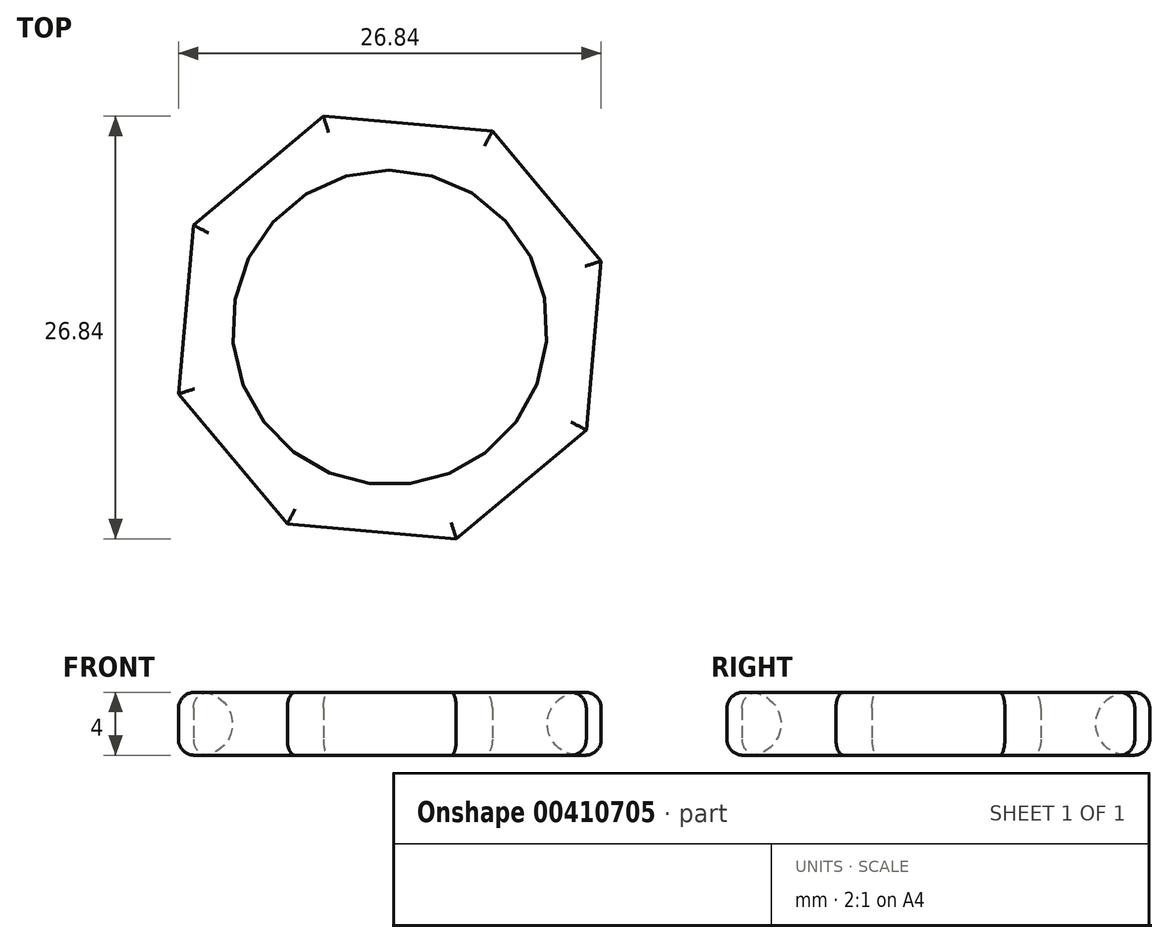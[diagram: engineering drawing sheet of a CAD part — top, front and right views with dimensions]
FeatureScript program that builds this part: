
annotation { "Feature Type Name" : "Feature", "Feature Type Description" : "" }
export const myFeature = defineFeature(function(context is Context, id is Id, definition is map)
    precondition{}
    {
        {
            var Q0;
            Q0=qCreatedBy(makeId("Top.planeOp"),FACE);
            var sketch = newSketch(context, id + "F0", { "sketchPlane" : qUnion([Q0])});
            skCircle(sketch, "E0.cCircle", {"center": v(0, 0) * mm, "radius": 13 * mm, "construction": true});
            skLineSegment(sketch, "E0.0", {"start": v(12.48, -6.5) * mm, "end": v(4.22, -13.42) * mm});
            skLineSegment(sketch, "E0.1", {"start": v(4.22, -13.42) * mm, "end": v(-6.5, -12.48) * mm});
            skLineSegment(sketch, "E0.2", {"start": v(-6.5, -12.48) * mm, "end": v(-13.42, -4.22) * mm});
            skLineSegment(sketch, "E0.3", {"start": v(-13.42, -4.22) * mm, "end": v(-12.48, 6.5) * mm});
            skLineSegment(sketch, "E0.4", {"start": v(-12.48, 6.5) * mm, "end": v(-4.22, 13.42) * mm});
            skLineSegment(sketch, "E0.5", {"start": v(-4.22, 13.42) * mm, "end": v(6.5, 12.48) * mm});
            skLineSegment(sketch, "E0.6", {"start": v(6.5, 12.48) * mm, "end": v(13.42, 4.22) * mm});
            skLineSegment(sketch, "E0.7", {"start": v(13.42, 4.22) * mm, "end": v(12.48, -6.5) * mm});
            skPoint(sketch, "E0.0.midPoint", {"position": v(8.35, -9.97) * mm});
            skCircle(sketch, "E1", {"center": v(0, 0) * mm, "radius": 10 * mm});
            skSolve(sketch);
        }
        {
            var Q0;
            Q0=makeQuery(id+"F0.imprint","IMPRINT",FACE,{"disambiguationData":[TD([[makeQuery(id+"F0.imprint","IMPRINT",EDGE,{"derivedFrom":sQuery(id+"F0.wireOp",EDGE,"E0.0")}),-1.0]])]});
            extrude(context, id + "F1", {"entities" : qUnion([Q0]), "depth" : 4 * mm});
        }
        {
            var Q0;
            Q0=makeQuery(id+"F1.opExtrude","CAP_EDGE",EDGE,{"disambiguationData":[OSD([sQuery(id+"F0.wireOp",EDGE,"E1")])],"isStart":true});
            var Q1;
            Q1=makeQuery(id+"F1.opExtrude","CAP_EDGE",EDGE,{"disambiguationData":[OSD([sQuery(id+"F0.wireOp",EDGE,"E1")])],"isStart":false});
            fillet(context, id + "F2", {"entities" : qUnion([Q0, Q1]), "radius" : 2 * mm, "tangentPropagation" : true, "allowEdgeOverflow" : false});
        }
        {
            var Q0;
            Q0=makeQuery(id+"F1.opExtrude","CAP_EDGE",EDGE,{"disambiguationData":[OSD([sQuery(id+"F0.wireOp",EDGE,"E0.5")])],"isStart":false});
            var Q1;
            Q1=makeQuery(id+"F1.opExtrude","CAP_EDGE",EDGE,{"disambiguationData":[OSD([sQuery(id+"F0.wireOp",EDGE,"E0.4")])],"isStart":false});
            var Q2;
            Q2=makeQuery(id+"F1.opExtrude","CAP_EDGE",EDGE,{"disambiguationData":[OSD([sQuery(id+"F0.wireOp",EDGE,"E0.3")])],"isStart":false});
            var Q3;
            Q3=makeQuery(id+"F1.opExtrude","CAP_EDGE",EDGE,{"disambiguationData":[OSD([sQuery(id+"F0.wireOp",EDGE,"E0.2")])],"isStart":false});
            var Q4;
            Q4=makeQuery(id+"F1.opExtrude","CAP_EDGE",EDGE,{"disambiguationData":[OSD([sQuery(id+"F0.wireOp",EDGE,"E0.1")])],"isStart":false});
            var Q5;
            Q5=makeQuery(id+"F1.opExtrude","CAP_EDGE",EDGE,{"disambiguationData":[OSD([sQuery(id+"F0.wireOp",EDGE,"E0.0")])],"isStart":false});
            var Q6;
            Q6=makeQuery(id+"F1.opExtrude","CAP_EDGE",EDGE,{"disambiguationData":[OSD([sQuery(id+"F0.wireOp",EDGE,"E0.7")])],"isStart":false});
            var Q7;
            Q7=makeQuery(id+"F1.opExtrude","CAP_EDGE",EDGE,{"disambiguationData":[OSD([sQuery(id+"F0.wireOp",EDGE,"E0.6")])],"isStart":false});
            var Q8;
            Q8=makeQuery(id+"F1.opExtrude","CAP_EDGE",EDGE,{"disambiguationData":[OSD([sQuery(id+"F0.wireOp",EDGE,"E0.6")])],"isStart":true});
            var Q9;
            Q9=makeQuery(id+"F1.opExtrude","CAP_EDGE",EDGE,{"disambiguationData":[OSD([sQuery(id+"F0.wireOp",EDGE,"E0.7")])],"isStart":true});
            var Q10;
            Q10=makeQuery(id+"F1.opExtrude","CAP_EDGE",EDGE,{"disambiguationData":[OSD([sQuery(id+"F0.wireOp",EDGE,"E0.0")])],"isStart":true});
            var Q11;
            Q11=makeQuery(id+"F1.opExtrude","CAP_EDGE",EDGE,{"disambiguationData":[OSD([sQuery(id+"F0.wireOp",EDGE,"E0.1")])],"isStart":true});
            var Q12;
            Q12=makeQuery(id+"F1.opExtrude","CAP_EDGE",EDGE,{"disambiguationData":[OSD([sQuery(id+"F0.wireOp",EDGE,"E0.2")])],"isStart":true});
            var Q13;
            Q13=makeQuery(id+"F1.opExtrude","CAP_EDGE",EDGE,{"disambiguationData":[OSD([sQuery(id+"F0.wireOp",EDGE,"E0.3")])],"isStart":true});
            var Q14;
            Q14=makeQuery(id+"F1.opExtrude","CAP_EDGE",EDGE,{"disambiguationData":[OSD([sQuery(id+"F0.wireOp",EDGE,"E0.4")])],"isStart":true});
            var Q15;
            Q15=makeQuery(id+"F1.opExtrude","CAP_EDGE",EDGE,{"disambiguationData":[OSD([sQuery(id+"F0.wireOp",EDGE,"E0.5")])],"isStart":true});
            fillet(context, id + "F3", {"entities" : qUnion([Q0, Q1, Q2, Q3, Q4, Q5, Q6, Q7, Q8, Q9, Q10, Q11, Q12, Q13, Q14, Q15]), "radius" : 1 * mm, "tangentPropagation" : true, "allowEdgeOverflow" : false});
        }
    });
